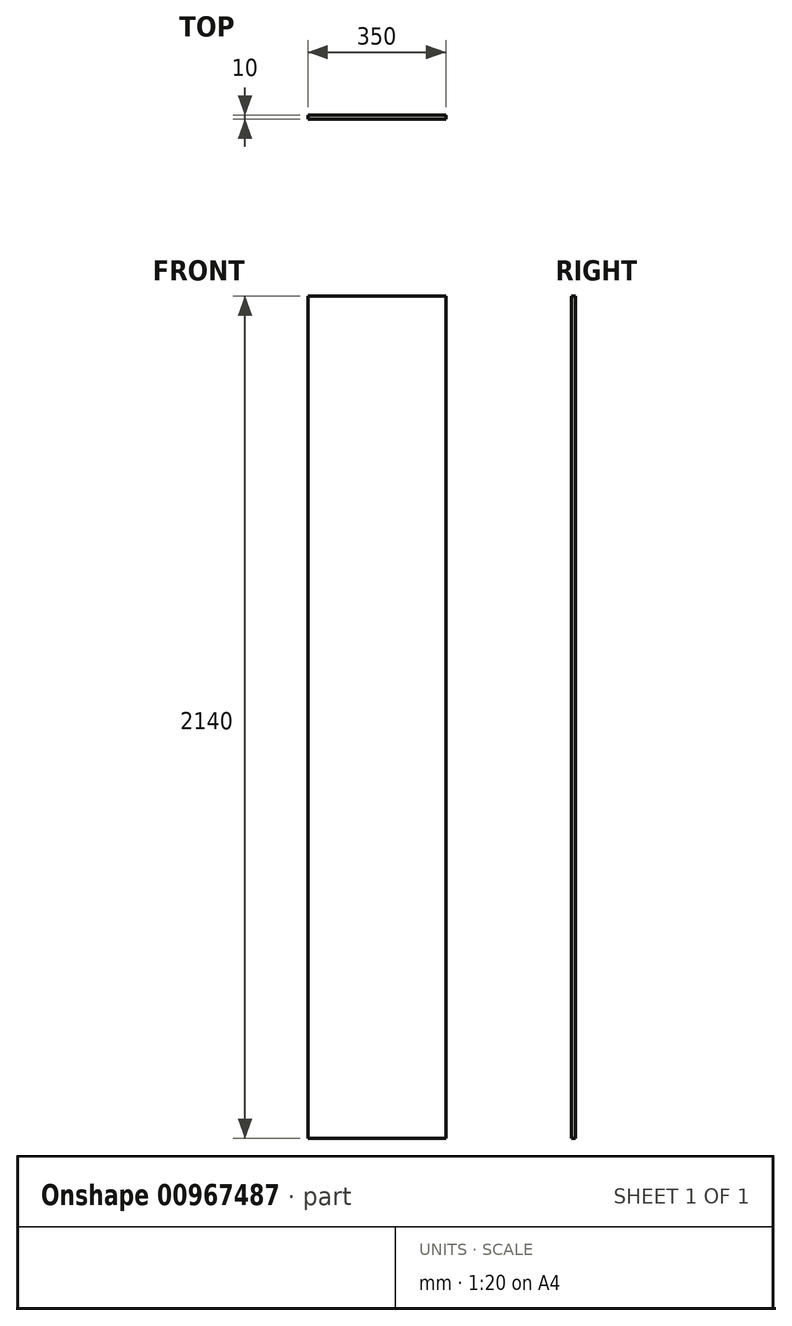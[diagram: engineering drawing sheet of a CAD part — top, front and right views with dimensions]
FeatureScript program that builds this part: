
annotation { "Feature Type Name" : "Feature", "Feature Type Description" : "" }
export const myFeature = defineFeature(function(context is Context, id is Id, definition is map)
    precondition{}
    {
        {
            var Q0;
            Q0=qCreatedBy(makeId("Front.planeOp"),FACE);
            var sketch = newSketch(context, id + "F0", { "sketchPlane" : qUnion([Q0])});
            skLineSegment(sketch, "E0.bottom", {"start": v(-175, 1070) * mm, "end": v(175, 1070) * mm});
            skLineSegment(sketch, "E0.top", {"start": v(-175, -1070) * mm, "end": v(175, -1070) * mm});
            skLineSegment(sketch, "E0.left", {"start": v(-175, 1070) * mm, "end": v(-175, -1070) * mm});
            skLineSegment(sketch, "E0.right", {"start": v(175, 1070) * mm, "end": v(175, -1070) * mm});
            skSolve(sketch);
        }
        {
            var Q0;
            Q0=makeQuery(id+"F0.imprint","IMPRINT",FACE,{"disambiguationData":[TD([[makeQuery(id+"F0.imprint","IMPRINT",EDGE,{"derivedFrom":sQuery(id+"F0.wireOp",EDGE,"E0.bottom")}),-1.0]])]});
            extrude(context, id + "F1", {"entities" : qUnion([Q0]), "depth" : 10 * mm, "offsetDistance" : 25 * mm});
        }
    });
